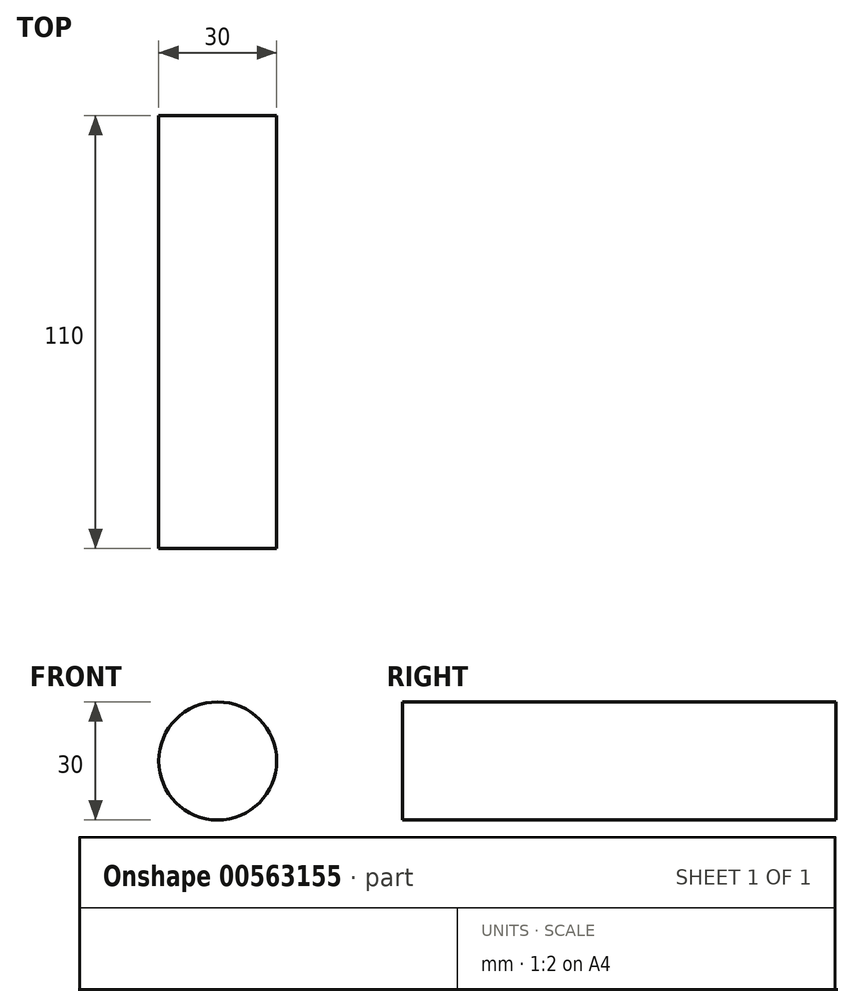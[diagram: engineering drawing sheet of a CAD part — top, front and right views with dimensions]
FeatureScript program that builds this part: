
annotation { "Feature Type Name" : "Feature", "Feature Type Description" : "" }
export const myFeature = defineFeature(function(context is Context, id is Id, definition is map)
    precondition{}
    {
        {
            var Q0;
            Q0=qCreatedBy(makeId("Front.planeOp"),FACE);
            var sketch = newSketch(context, id + "F0", { "sketchPlane" : qUnion([Q0])});
            skCircle(sketch, "E0", {"center": v(0, 0) * mm, "radius": 15 * mm});
            skSolve(sketch);
        }
        {
            var Q0;
            Q0 = qSketchRegion(id + "F0", true);
            extrude(context, id + "F1", {"entities" : qUnion([Q0]), "depth" : 110 * mm, "offsetDistance" : 25 * mm});
        }
    });
